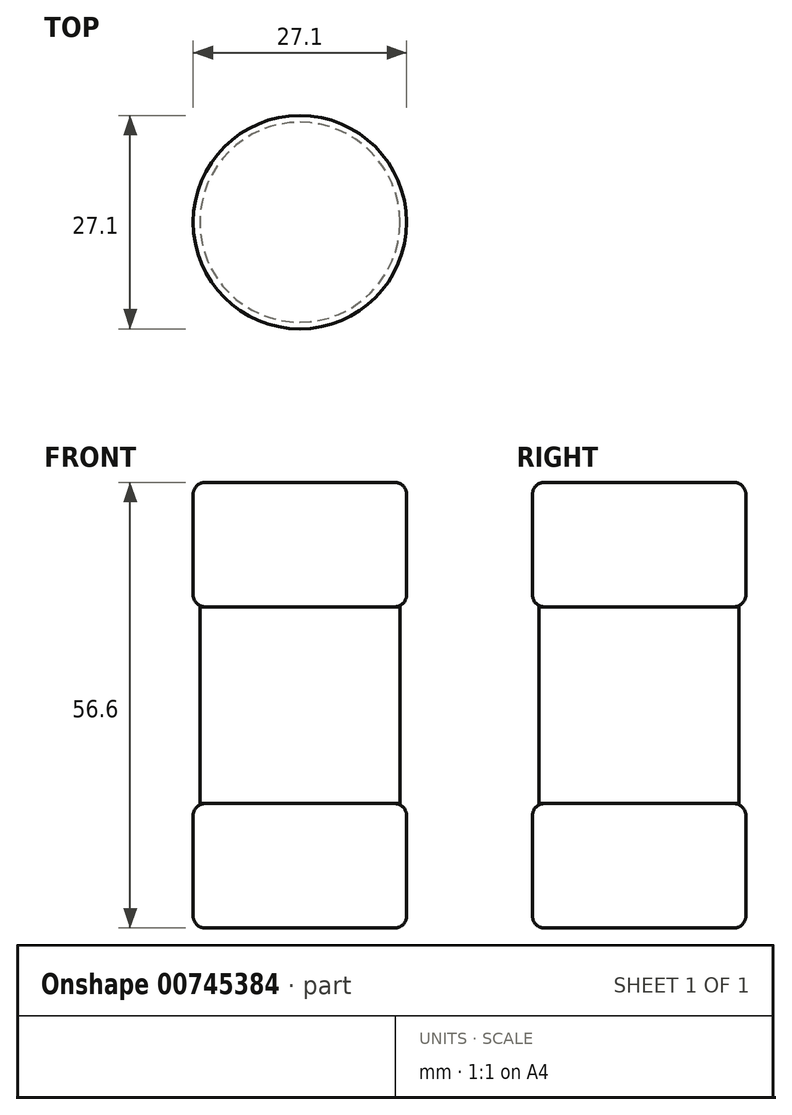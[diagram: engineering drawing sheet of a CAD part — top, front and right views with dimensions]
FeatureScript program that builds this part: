
annotation { "Feature Type Name" : "Feature", "Feature Type Description" : "" }
export const myFeature = defineFeature(function(context is Context, id is Id, definition is map)
    precondition{}
    {
        {
            var Q0;
            Q0=qCreatedBy(makeId("Top.planeOp"),FACE);
            var sketch = newSketch(context, id + "F0", { "sketchPlane" : qUnion([Q0])});
            skCircle(sketch, "E0", {"center": v(0, 0) * mm, "radius": 13.55 * mm});
            skSolve(sketch);
        }
        {
            var Q0;
            Q0 = qSketchRegion(id + "F0", true);
            extrude(context, id + "F1", {"entities" : qUnion([Q0]), "depth" : 15.8 * mm, "offsetDistance" : 25 * mm});
        }
        {
            var Q0;
            Q0=makeQuery(id+"F1.opExtrude","CAP_FACE",FACE,{"disambiguationData":[OSD([sQuery(id+"F0.wireOp",EDGE,"E0")])],"isStart":false});
            var sketch = newSketch(context, id + "F2", { "sketchPlane" : qUnion([Q0])});
            skCircle(sketch, "E1", {"center": v(0, 0) * mm, "radius": 12.7 * mm});
            skSolve(sketch);
        }
        {
            var Q0;
            Q0 = qSketchRegion(id + "F2", true);
            extrude(context, id + "F3", {"entities" : qUnion([Q0]), "depth" : 25 * mm, "offsetDistance" : 25 * mm});
        }
        {
            var Q0;
            Q0=makeQuery(id+"F3.opExtrude","CAP_FACE",FACE,{"disambiguationData":[OSD([sQuery(id+"F2.wireOp",EDGE,"E1")])],"isStart":false});
            var sketch = newSketch(context, id + "F4", { "sketchPlane" : qUnion([Q0])});
            skCircle(sketch, "E2", {"center": v(0, 0) * mm, "radius": 13.55 * mm});
            skSolve(sketch);
        }
        {
            var Q0;
            Q0 = qSketchRegion(id + "F4", true);
            extrude(context, id + "F5", {"entities" : qUnion([Q0]), "depth" : 15.8 * mm, "offsetDistance" : 25 * mm});
        }
        {
            var Q0;
            Q0=makeQuery(id+"F5.opExtrude","CAP_EDGE",EDGE,{"disambiguationData":[OSD([sQuery(id+"F4.wireOp",EDGE,"E2")])],"isStart":false});
            var Q1;
            Q1=makeQuery(id+"F1.opExtrude","CAP_EDGE",EDGE,{"disambiguationData":[OSD([sQuery(id+"F0.wireOp",EDGE,"E0")])],"isStart":true});
            var Q2;
            Q2=makeQuery(id+"F5.opExtrude","CAP_EDGE",EDGE,{"disambiguationData":[OSD([sQuery(id+"F4.wireOp",EDGE,"E2")])],"isStart":true});
            var Q3;
            Q3=makeQuery(id+"F1.opExtrude","CAP_EDGE",EDGE,{"disambiguationData":[OSD([sQuery(id+"F0.wireOp",EDGE,"E0")])],"isStart":false});
            fillet(context, id + "F6", {"entities" : qUnion([Q0, Q1, Q2, Q3]), "radius" : 1.5 * mm, "tangentPropagation" : true, "allowEdgeOverflow" : false});
        }
    });
